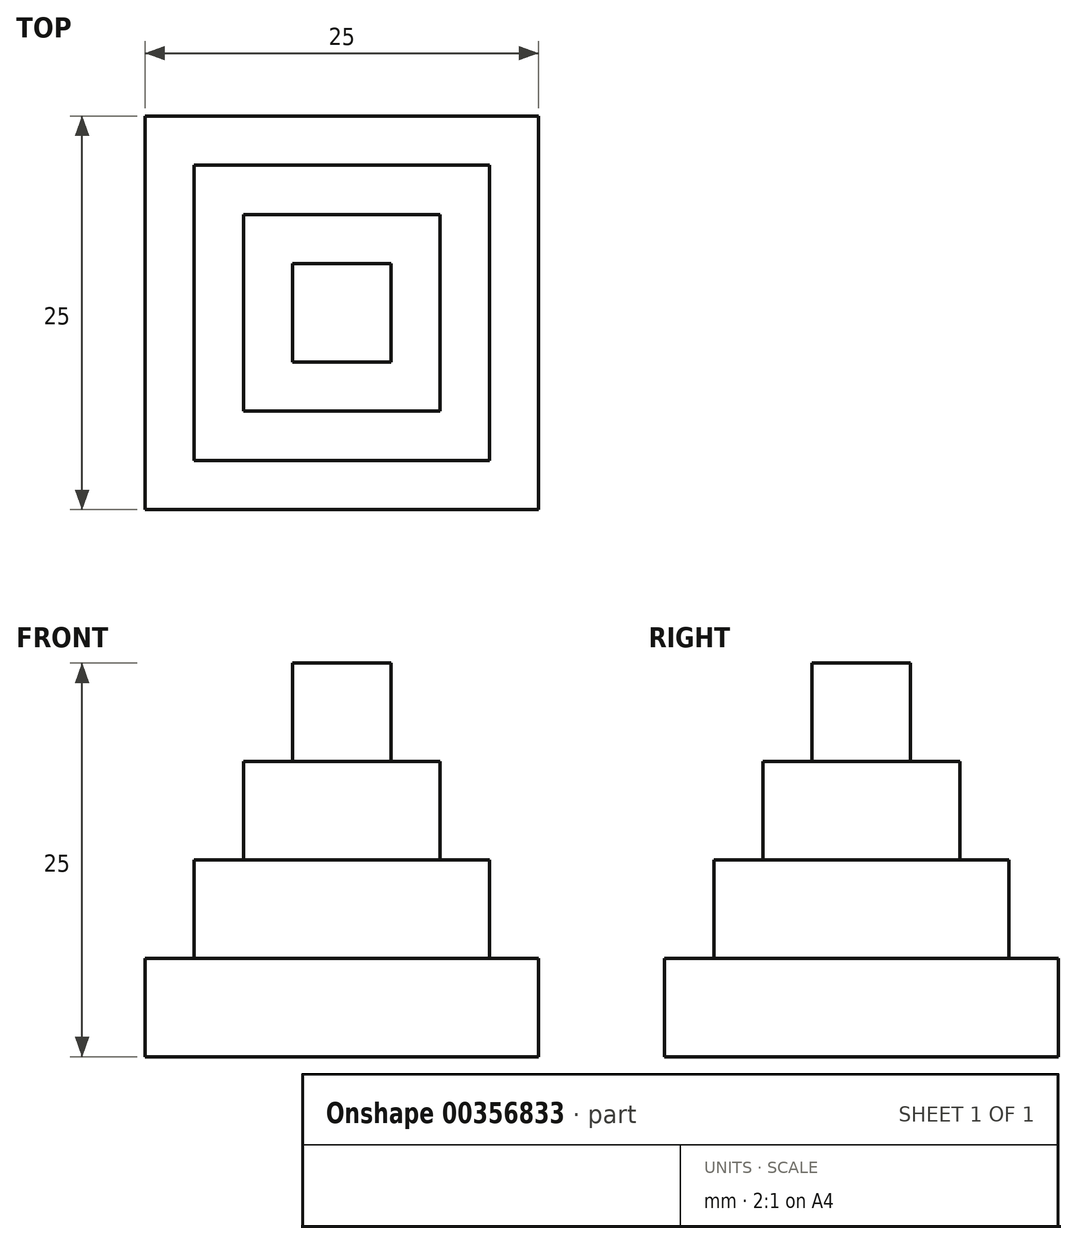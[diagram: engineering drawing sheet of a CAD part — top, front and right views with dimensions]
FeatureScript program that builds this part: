
annotation { "Feature Type Name" : "Feature", "Feature Type Description" : "" }
export const myFeature = defineFeature(function(context is Context, id is Id, definition is map)
    precondition{}
    {
        {
            assignVariable(context, id + "F0", {"name" : "Size", "anyValue" : 25});
        }
        {
            var Q0;
            Q0=qCreatedBy(makeId("Top.planeOp"),FACE);
            var sketch = newSketch(context, id + "F1", { "sketchPlane" : qUnion([Q0])});
            skLineSegment(sketch, "E0.bottom", {"start": v(0, 0) * mm, "end": v(25, 0) * mm});
            skLineSegment(sketch, "E0.top", {"start": v(0, 25) * mm, "end": v(25, 25) * mm});
            skLineSegment(sketch, "E0.left", {"start": v(0, 0) * mm, "end": v(0, 25) * mm});
            skLineSegment(sketch, "E0.right", {"start": v(25, 0) * mm, "end": v(25, 25) * mm});
            skLineSegment(sketch, "E1.0", {"start": v(3.12, 21.88) * mm, "end": v(21.87, 21.88) * mm});
            skLineSegment(sketch, "E1.1", {"start": v(3.12, 3.12) * mm, "end": v(3.12, 21.88) * mm});
            skLineSegment(sketch, "E1.2", {"start": v(3.12, 3.12) * mm, "end": v(21.88, 3.12) * mm});
            skLineSegment(sketch, "E1.3", {"start": v(21.88, 3.12) * mm, "end": v(21.87, 21.88) * mm});
            skLineSegment(sketch, "E2.0", {"start": v(6.25, 18.75) * mm, "end": v(18.75, 18.75) * mm});
            skLineSegment(sketch, "E2.1", {"start": v(6.25, 6.25) * mm, "end": v(6.25, 18.75) * mm});
            skLineSegment(sketch, "E2.2", {"start": v(6.25, 6.25) * mm, "end": v(18.75, 6.25) * mm});
            skLineSegment(sketch, "E2.3", {"start": v(18.75, 6.25) * mm, "end": v(18.75, 18.75) * mm});
            skLineSegment(sketch, "E3.0", {"start": v(9.37, 15.63) * mm, "end": v(15.62, 15.63) * mm});
            skLineSegment(sketch, "E3.1", {"start": v(9.37, 9.37) * mm, "end": v(9.37, 15.63) * mm});
            skLineSegment(sketch, "E3.2", {"start": v(9.37, 9.37) * mm, "end": v(15.62, 9.37) * mm});
            skLineSegment(sketch, "E3.3", {"start": v(15.62, 9.37) * mm, "end": v(15.62, 15.63) * mm});
            skSolve(sketch);
        }
        {
            var Q0;
            Q0=makeQuery(id+"F1.imprint","IMPRINT",FACE,{"disambiguationData":[TD([[makeQuery(id+"F1.imprint","IMPRINT",EDGE,{"derivedFrom":sQuery(id+"F1.wireOp",EDGE,"E0.bottom")}),1.0]])]});
            extrude(context, id + "F2", {"entities" : qUnion([Q0]), "depth" : (getVariable(context, 'Size') * 0.25) * mm});
        }
        {
            var Q0;
            Q0=makeQuery(id+"F1.imprint","IMPRINT",FACE,{"disambiguationData":[TD([[makeQuery(id+"F1.imprint","IMPRINT",EDGE,{"derivedFrom":sQuery(id+"F1.wireOp",EDGE,"E1.0")}),-1.0]])]});
            extrude(context, id + "F3", {"entities" : qUnion([Q0]), "operationType" : NewBodyOperationType.ADD, "depth" : (getVariable(context, 'Size') * 0.5) * mm});
        }
        {
            var Q0;
            Q0=makeQuery(id+"F1.imprint","IMPRINT",FACE,{"disambiguationData":[TD([[makeQuery(id+"F1.imprint","IMPRINT",EDGE,{"derivedFrom":sQuery(id+"F1.wireOp",EDGE,"E2.0")}),-1.0]])]});
            extrude(context, id + "F4", {"entities" : qUnion([Q0]), "operationType" : NewBodyOperationType.ADD, "depth" : (getVariable(context, 'Size') * 0.75) * mm});
        }
        {
            var Q0;
            Q0=makeQuery(id+"F1.imprint","IMPRINT",FACE,{"disambiguationData":[TD([[makeQuery(id+"F1.imprint","IMPRINT",EDGE,{"derivedFrom":sQuery(id+"F1.wireOp",EDGE,"E3.0")}),-1.0]])]});
            extrude(context, id + "F5", {"entities" : qUnion([Q0]), "operationType" : NewBodyOperationType.ADD, "depth" : (getVariable(context, 'Size')) * mm});
        }
    });
